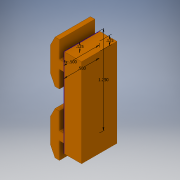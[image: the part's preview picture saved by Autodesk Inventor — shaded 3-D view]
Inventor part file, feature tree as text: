
AUTODESK INVENTOR PART (.ipt)
format: ipt  version: 2017 (Build 210142000, 142)  size: 158,720 bytes
history: native  units: in
note: dims shown in document units (in); Inventor stores cm internally (conversion verified against a paired STEP export)
features: extrude x4, sketch x3, plane x1, mirror x1
ambient origin geometry x8: Origin, YZ Plane, XZ Plane, XY Plane, X Axis, Y Axis, Z Axis, Center Point
bodies: Solid1 (feature_tree)
feature tree (9):
  sketch  "Sketch1"  dims[d0=1.25in d1=0.5in]
  extrude  "Extrusion1"  Depth=0.5in
  extrude  "Extrusion2"  Depth=0.125in
  extrude  "Extrusion3"  Depth=0.125in
  extrude  "Extrusion4"  Depth=0.0625in TaperAngle=0.0deg
  plane  "Work Plane3"
  mirror  "Mirror1"
  sketch  "Sketch2"  dims[d2=0.25in d3=0.0in d4=0.125in]
  sketch  "Sketch3"  dims[d5=0.5in d6=0.125in d7=0.0625in d8=0.0in d9=0.5in d10=0.0in d11=0.24in d12=0.24in d13=0.125in d14=0.0in d16=0.125in d17=0.062in d18=0.062in d19=0.125in d20=0.125in d21=0.0in]
